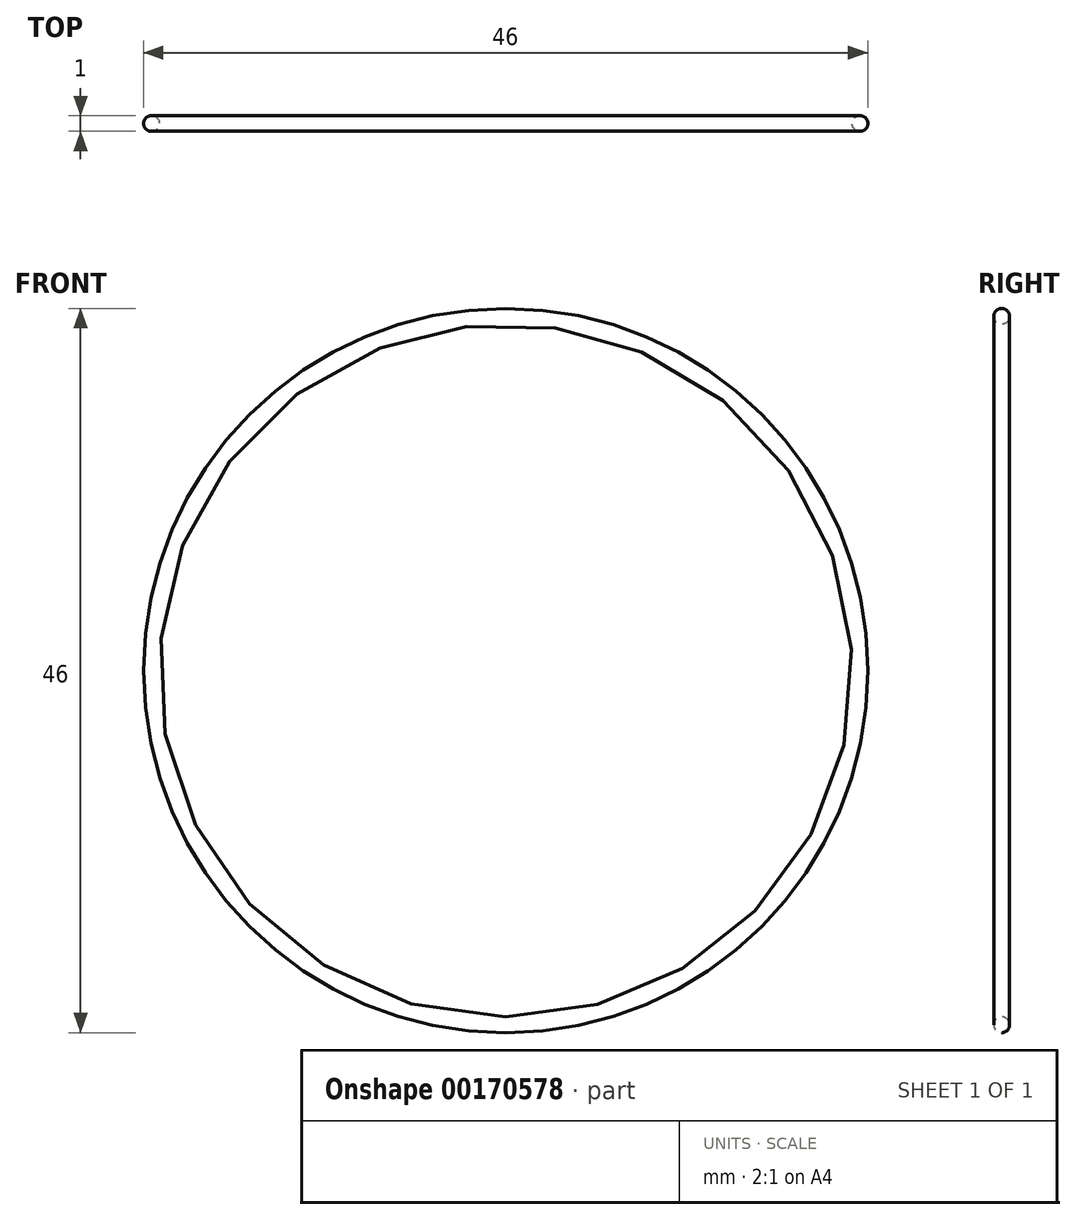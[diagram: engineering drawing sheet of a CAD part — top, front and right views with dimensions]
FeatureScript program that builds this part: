
annotation { "Feature Type Name" : "Feature", "Feature Type Description" : "" }
export const myFeature = defineFeature(function(context is Context, id is Id, definition is map)
    precondition{}
    {
        {
            var Q0;
            Q0=qCreatedBy(makeId("Top.planeOp"),FACE);
            var sketch = newSketch(context, id + "F0", { "sketchPlane" : qUnion([Q0])});
            skCircle(sketch, "E0", {"center": v(-22.5, 0) * mm, "radius": 0.5 * mm});
            skLineSegment(sketch, "E1", {"start": v(0, 0) * mm, "end": v(0, 8.88) * mm});
            skSolve(sketch);
        }
        {
            var Q0;
            Q0 = qSketchRegion(id + "F0", true);
            var Q1;
            Q1=sQuery(id+"F0.wireOp",EDGE,"E1");
            revolve(context, id + "F1", {"entities" : qUnion([Q0]), "axis" : qUnion([Q1]), "revolveType" : RevolveType.FULL});
        }
    });
